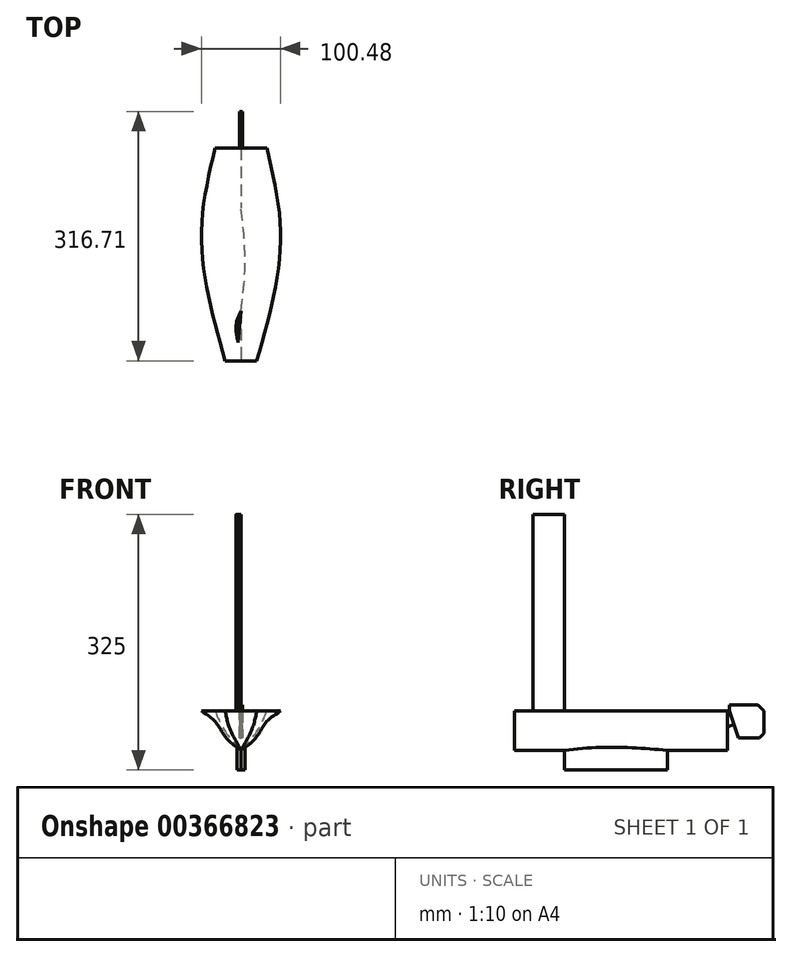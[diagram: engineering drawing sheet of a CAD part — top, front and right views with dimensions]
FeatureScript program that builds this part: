
annotation { "Feature Type Name" : "Feature", "Feature Type Description" : "" }
export const myFeature = defineFeature(function(context is Context, id is Id, definition is map)
    precondition{}
    {
        {
            var Q0;
            Q0=qCreatedBy(makeId("Front.planeOp"),FACE);
            cPlane(context, id + "F0", {"entities" : qUnion([Q0]), "cplaneType" : CPlaneType.OFFSET, "offset" : 100 * mm, "width" : 150 * mm, "height" : 150 * mm});
        }
        {
            var Q0;
            Q0=qCreatedBy(makeId("Front.planeOp"),FACE);
            cPlane(context, id + "F1", {"entities" : qUnion([Q0]), "cplaneType" : CPlaneType.OFFSET, "offset" : 270 * mm, "width" : 150 * mm, "height" : 150 * mm});
        }
        {
            var Q0;
            Q0=qCreatedBy(makeId("Front.planeOp"),FACE);
            var sketch = newSketch(context, id + "F2", { "sketchPlane" : qUnion([Q0])});
            skLineSegment(sketch, "E0", {"start": v(0, 0) * mm, "end": v(0, -50) * mm});
            skLineSegment(sketch, "E1", {"start": v(0, 0) * mm, "end": v(50, 0) * mm});
            skPoint(sketch, "E2.1.internal.snap0", {"position": v(25, 0) * mm});
            skFitSpline(sketch, "E3", {"points": [v(0, -50) * mm, v(21.28, -24.33) * mm, v(32.93, 0) * mm], "startDerivative": vector(44.58, 48.08) * mm, "endDerivative": vector(20.86, 52) * mm});
            skSolve(sketch);
        }
        {
            var Q0;
            Q0=qCreatedBy(id+"F0.planeOp",FACE);
            var sketch = newSketch(context, id + "F3", { "sketchPlane" : qUnion([Q0])});
            skLineSegment(sketch, "E4", {"start": v(0, 0) * mm, "end": v(0, -50) * mm});
            skLineSegment(sketch, "E5", {"start": v(0, 0) * mm, "end": v(50, 0) * mm});
            skFitSpline(sketch, "E6", {"points": [v(0, -50) * mm, v(20.01, -32.64) * mm, v(31.92, -14.36) * mm, v(50, 0) * mm], "startDerivative": vector(63.52, 46.2) * mm, "endDerivative": vector(61.05, 39.55) * mm});
            skSolve(sketch);
        }
        {
            var Q0;
            Q0=qCreatedBy(id+"F1.planeOp",FACE);
            var sketch = newSketch(context, id + "F4", { "sketchPlane" : qUnion([Q0])});
            skLineSegment(sketch, "E7", {"start": v(0, 0) * mm, "end": v(0, -50) * mm});
            skLineSegment(sketch, "E8", {"start": v(0, 0) * mm, "end": v(20, 0) * mm});
            skFitSpline(sketch, "E9", {"points": [v(0, -50) * mm, v(14.68, -21) * mm, v(20, 0) * mm], "startDerivative": vector(30.74, 54.3) * mm, "endDerivative": vector(8.51, 45.4) * mm});
            skSolve(sketch);
        }
        {
            var Q0;
            Q0=makeQuery(id+"F2.imprint","IMPRINT",FACE,{"disambiguationData":[TD([[makeQuery(id+"F2.imprint","IMPRINT",EDGE,{"derivedFrom":sQuery(id+"F2.wireOp",EDGE,"E0")}),1.0]])]});
            var Q1;
            Q1=makeQuery(id+"F3.imprint","IMPRINT",FACE,{"disambiguationData":[TD([[makeQuery(id+"F3.imprint","IMPRINT",EDGE,{"derivedFrom":sQuery(id+"F3.wireOp",EDGE,"E4")}),1.0]])]});
            var Q2;
            Q2=makeQuery(id+"F4.imprint","IMPRINT",FACE,{"disambiguationData":[TD([[makeQuery(id+"F4.imprint","IMPRINT",EDGE,{"derivedFrom":sQuery(id+"F4.wireOp",EDGE,"E7")}),1.0]])]});
            loft(context, id + "F5", {"sheetProfilesArray" : [{ "sheetProfileEntities" : qUnion([Q0]) }, { "sheetProfileEntities" : qUnion([Q1]) }, { "sheetProfileEntities" : qUnion([Q2]) }]});
        }
        {
            var Q0;
            Q0=makeQuery(id+"F5.opLoft","SWEPT_BODY",BODY,{"disambiguationData":[OSD([makeQuery(id+"F2.imprint","IMPRINT",FACE,{"disambiguationData":[TD([[makeQuery(id+"F2.imprint","IMPRINT",EDGE,{"derivedFrom":sQuery(id+"F2.wireOp",EDGE,"E0")}),1.0]])]}),sQuery(id+"F3.wireOp",EDGE,"E4"),makeQuery(id+"F4.imprint","IMPRINT",FACE,{"disambiguationData":[TD([[makeQuery(id+"F4.imprint","IMPRINT",EDGE,{"derivedFrom":sQuery(id+"F4.wireOp",EDGE,"E7")}),1.0]])]})])]});
            var Q1;
            {var subQ0=sQuery(id+"F3.wireOp",EDGE,"E4");var subQ1=sQuery(id+"F3.wireOp",EDGE,"b7cb7ae5-a023-4945-9d34-2c9c8fd4177d");var subQ2=sQuery(id+"F3.wireOp",EDGE,"E5");var subQ3=sQuery(id+"F2.wireOp",EDGE,"E0");var subQ4=sQuery(id+"F2.wireOp",EDGE,"8e8e072c-9e5d-4a9f-a3a8-de189503a9bf");var subQ5=sQuery(id+"F2.wireOp",EDGE,"E1");Q1=makeQuery(id+"F5.opLoft","SWEPT_FACE",FACE,{"disambiguationData":[OSD([subQ3,subQ5,subQ4,subQ0,subQ2,subQ1]),TDD([makeQuery(id+"F2.imprint","INTERSECT",VERTEX,{"derivedFrom":[subQ3,subQ5]}),makeQuery(id+"F2.imprint","INTERSECT",VERTEX,{"derivedFrom":[subQ3,subQ4]}),makeQuery(id+"F2.imprint","IMPRINT",EDGE,{"derivedFrom":subQ3}),makeQuery(id+"F3.imprint","INTERSECT",VERTEX,{"derivedFrom":[subQ0,subQ2]}),makeQuery(id+"F3.imprint","INTERSECT",VERTEX,{"derivedFrom":[subQ0,subQ1]}),makeQuery(id+"F3.imprint","IMPRINT",EDGE,{"derivedFrom":subQ0})])]});}
            mirror(context, id + "F6", {"operationType" : NewBodyOperationType.ADD, "entities" : qUnion([Q0]), "mirrorPlane" : qUnion([Q1])});
        }
        {
            var Q0;
            {var subQ0=sQuery(id+"F3.wireOp",EDGE,"E5");var subQ1=sQuery(id+"F3.wireOp",EDGE,"E6");var subQ2=sQuery(id+"F3.wireOp",EDGE,"E4");var subQ3=sQuery(id+"F2.wireOp",EDGE,"E1");var subQ4=sQuery(id+"F2.wireOp",EDGE,"E0");var subQ5=makeQuery(id+"F2.imprint","INTERSECT",VERTEX,{"derivedFrom":[subQ4,subQ3]});var subQ6=sQuery(id+"F2.wireOp",EDGE,"E3");var subQ7=makeQuery(id+"F2.imprint","INTERSECT",VERTEX,{"derivedFrom":[subQ3,subQ6]});var subQ8=makeQuery(id+"F5.opLoft","SWEPT_FACE",FACE,{"disambiguationData":[OSD([subQ4,subQ3,subQ6,subQ2,subQ0,subQ1]),TDD([subQ5,subQ7,makeQuery(id+"F2.imprint","IMPRINT",EDGE,{"disambiguationData":[TD([[subQ5,-1.0]])],"derivedFrom":subQ3}),makeQuery(id+"F3.imprint","INTERSECT",VERTEX,{"derivedFrom":[subQ2,subQ0]}),makeQuery(id+"F3.imprint","INTERSECT",VERTEX,{"derivedFrom":[subQ0,subQ1]}),makeQuery(id+"F3.imprint","IMPRINT",EDGE,{"derivedFrom":subQ0})])]});Q0=makeQuery(id+"F6.boolean.opBoolean","MERGE",FACE,{"derivedFrom":[subQ8,makeQuery(id+"F6.opPattern","COPY",FACE,{"derivedFrom":subQ8,"instanceName":"1"})]});}
            var sketch = newSketch(context, id + "F7", { "sketchPlane" : qUnion([Q0])});
            skLineSegment(sketch, "E10", {"start": v(0, -206.5) * mm, "end": v(0, -75.75) * mm});
            skFitSpline(sketch, "E11", {"points": [v(0, -75.75) * mm, v(-3.82, -111.2) * mm, v(-4.8, -158.98) * mm, v(0, -206.5) * mm], "startDerivative": vector(-14.07, -112.7) * mm, "endDerivative": vector(17.5, -134.55) * mm});
            skFitSpline(sketch, "E12", {"points": [v(0, -206.5) * mm, v(-4.46, -216.62) * mm, v(-6.17, -229.65) * mm, v(-3.56, -247.05) * mm], "startDerivative": vector(-16.67, -32.72) * mm, "endDerivative": vector(9.7, -47.54) * mm});
            skLineSegment(sketch, "E13", {"start": v(-3.56, -247.05) * mm, "end": v(0, -206.5) * mm});
            skSolve(sketch);
        }
        {
            var Q0;
            Q0=makeQuery(id+"F7.imprint","IMPRINT",FACE,{"disambiguationData":[TD([[makeQuery(id+"F7.imprint","IMPRINT",EDGE,{"derivedFrom":sQuery(id+"F7.wireOp",EDGE,"E10")}),1.0]])]});
            extrude(context, id + "F8", {"entities" : qUnion([Q0]), "operationType" : NewBodyOperationType.ADD, "oppositeDirection" : true, "depth" : 75 * mm});
        }
        {
            var Q0;
            {var subQ0=sQuery(id+"F2.wireOp",EDGE,"E0");Q0=makeQuery(id+"F5.opLoft","SWEPT_BODY",BODY,{"disambiguationData":[OSD([makeQuery(id+"F2.imprint","IMPRINT",FACE,{"disambiguationData":[TD([[makeQuery(id+"F2.imprint","IMPRINT",EDGE,{"derivedFrom":subQ0}),1.0]])]}),sQuery(id+"F3.wireOp",EDGE,"E4"),makeQuery(id+"F4.imprint","IMPRINT",FACE,{"disambiguationData":[TD([[makeQuery(id+"F4.imprint","IMPRINT",EDGE,{"derivedFrom":sQuery(id+"F4.wireOp",EDGE,"E7")}),1.0]])]})])]});}
            var Q1;
            Q1=makeQuery(id+"F8.opExtrude","SWEPT_FACE",FACE,{"disambiguationData":[OSD([sQuery(id+"F7.wireOp",EDGE,"E10")])]});
            mirror(context, id + "F9", {"operationType" : NewBodyOperationType.ADD, "entities" : qUnion([Q0]), "mirrorPlane" : qUnion([Q1])});
        }
        {
            var Q0;
            Q0=qCreatedBy(makeId("Right.planeOp"),FACE);
            var sketch = newSketch(context, id + "F10", { "sketchPlane" : qUnion([Q0])});
            skLineSegment(sketch, "E14", {"start": v(3, 0) * mm, "end": v(3, 7.53) * mm});
            skLineSegment(sketch, "E15", {"start": v(3, 7.53) * mm, "end": v(39.18, 7.53) * mm});
            skLineSegment(sketch, "E16", {"start": v(39.18, 7.53) * mm, "end": v(46.7, 0) * mm});
            skLineSegment(sketch, "E17", {"start": v(46.7, 0) * mm, "end": v(46.7, -28.32) * mm});
            skLineSegment(sketch, "E18", {"start": v(46.7, -28.32) * mm, "end": v(40.99, -34.34) * mm});
            skLineSegment(sketch, "E19", {"start": v(40.99, -34.34) * mm, "end": v(14.47, -34.34) * mm});
            skLineSegment(sketch, "E20", {"start": v(14.47, -34.34) * mm, "end": v(3, 0) * mm});
            skLineSegment(sketch, "E21", {"start": v(0, 0) * mm, "end": v(3, 0) * mm});
            skLineSegment(sketch, "E22", {"start": v(8.74, -17.17) * mm, "end": v(0, -20) * mm});
            skLineSegment(sketch, "E23", {"start": v(0, -20) * mm, "end": v(0, 0) * mm});
            skSolve(sketch);
        }
        {
            var Q0;
            {var subQ0=sQuery(id+"F10.wireOp",EDGE,"E14");Q0=makeQuery(id+"F10.imprint","IMPRINT",FACE,{"disambiguationData":[TD([[makeQuery(id+"F10.imprint","IMPRINT",EDGE,{"derivedFrom":subQ0}),-1.0]])]});}
            extrude(context, id + "F11", {"entities" : qUnion([Q0]), "depth" : 2 * mm});
        }
        {
            var Q0;
            Q0=makeQuery(id+"F11.opExtrude","SWEPT_BODY",BODY,{"disambiguationData":[OSD([sQuery(id+"F10.wireOp",EDGE,"E14"),sQuery(id+"F10.wireOp",EDGE,"E15"),sQuery(id+"F10.wireOp",EDGE,"E16"),sQuery(id+"F10.wireOp",EDGE,"E17"),sQuery(id+"F10.wireOp",EDGE,"E18"),sQuery(id+"F10.wireOp",EDGE,"E19"),sQuery(id+"F10.wireOp",EDGE,"E20")])]});
            var Q1;
            Q1=makeQuery(id+"F11.opExtrude","CAP_FACE",FACE,{"disambiguationData":[OSD([sQuery(id+"F10.wireOp",EDGE,"E14"),sQuery(id+"F10.wireOp",EDGE,"E15"),sQuery(id+"F10.wireOp",EDGE,"E16"),sQuery(id+"F10.wireOp",EDGE,"E17"),sQuery(id+"F10.wireOp",EDGE,"E18"),sQuery(id+"F10.wireOp",EDGE,"E19"),sQuery(id+"F10.wireOp",EDGE,"E20")])],"isStart":true});
            mirror(context, id + "F12", {"operationType" : NewBodyOperationType.ADD, "entities" : qUnion([Q0]), "mirrorPlane" : qUnion([Q1])});
        }
        {
            var Q0;
            {var subQ0=sQuery(id+"F10.wireOp",EDGE,"E21");Q0=makeQuery(id+"F10.imprint","IMPRINT",FACE,{"disambiguationData":[TD([[makeQuery(id+"F10.imprint","IMPRINT",EDGE,{"derivedFrom":subQ0}),-1.0]])]});}
            extrude(context, id + "F13", {"entities" : qUnion([Q0]), "depth" : 1 * mm});
        }
        {
            var Q0;
            Q0=makeQuery(id+"F13.opExtrude","SWEPT_BODY",BODY,{"disambiguationData":[OSD([sQuery(id+"F10.wireOp",EDGE,"E20"),sQuery(id+"F10.wireOp",EDGE,"E21"),sQuery(id+"F10.wireOp",EDGE,"E22"),sQuery(id+"F10.wireOp",EDGE,"E23")])]});
            var Q1;
            Q1=makeQuery(id+"F13.opExtrude","CAP_FACE",FACE,{"disambiguationData":[OSD([sQuery(id+"F10.wireOp",EDGE,"E20"),sQuery(id+"F10.wireOp",EDGE,"E21"),sQuery(id+"F10.wireOp",EDGE,"E22"),sQuery(id+"F10.wireOp",EDGE,"E23")])],"isStart":true});
            mirror(context, id + "F14", {"entities" : qUnion([Q0]), "mirrorPlane" : qUnion([Q1])});
        }
        {
            var Q0;
            Q0=makeQuery(id+"F7.imprint","IMPRINT",FACE,{"disambiguationData":[TD([[makeQuery(id+"F7.imprint","IMPRINT",EDGE,{"derivedFrom":sQuery(id+"F7.wireOp",EDGE,"E12")}),1.0]])]});
            extrude(context, id + "F15", {"entities" : qUnion([Q0]), "operationType" : NewBodyOperationType.ADD, "depth" : 250 * mm});
        }
    });
